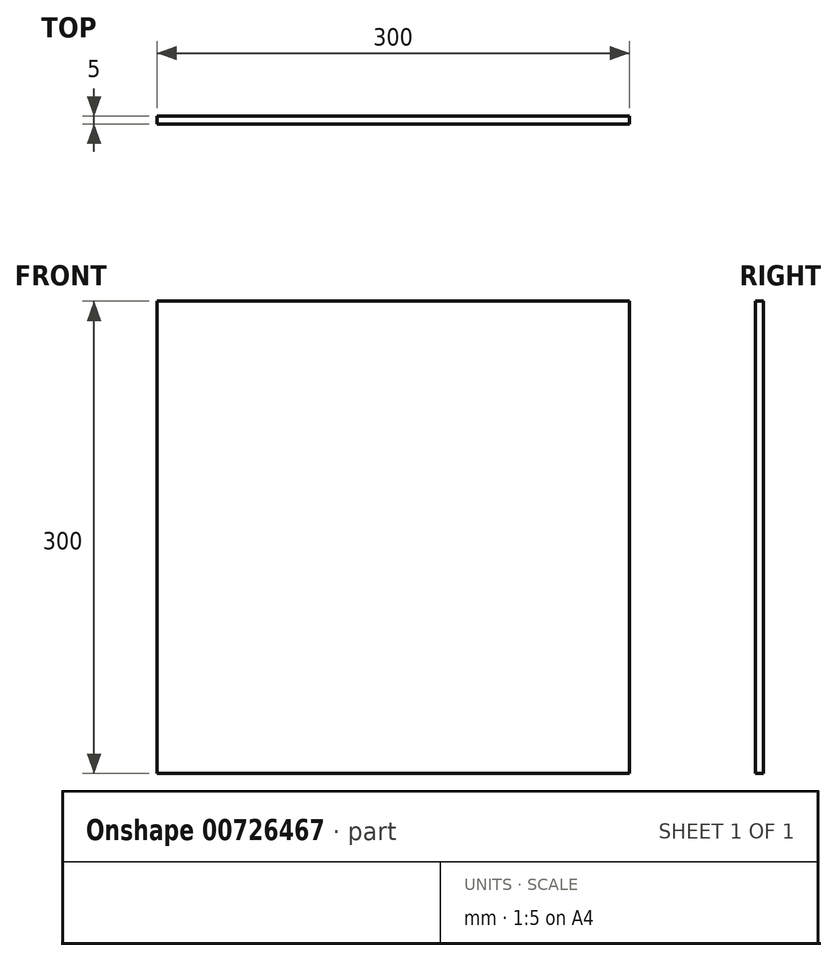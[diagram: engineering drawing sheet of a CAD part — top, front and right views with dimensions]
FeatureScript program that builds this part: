
annotation { "Feature Type Name" : "Feature", "Feature Type Description" : "" }
export const myFeature = defineFeature(function(context is Context, id is Id, definition is map)
    precondition{}
    {
        {
            var Q0;
            Q0=qCreatedBy(makeId("Front.planeOp"),FACE);
            var sketch = newSketch(context, id + "F0", { "sketchPlane" : qUnion([Q0])});
            skLineSegment(sketch, "E0.bottom", {"start": v(0, 0) * mm, "end": v(300, 0) * mm});
            skLineSegment(sketch, "E0.top", {"start": v(0, 300) * mm, "end": v(300, 300) * mm});
            skLineSegment(sketch, "E0.left", {"start": v(0, 0) * mm, "end": v(0, 300) * mm});
            skLineSegment(sketch, "E0.right", {"start": v(300, 0) * mm, "end": v(300, 300) * mm});
            skSolve(sketch);
        }
        {
            var Q0;
            Q0=makeQuery(id+"F0.imprint","IMPRINT",FACE,{"disambiguationData":[TD([[makeQuery(id+"F0.imprint","IMPRINT",EDGE,{"derivedFrom":sQuery(id+"F0.wireOp",EDGE,"E0.bottom")}),1.0]])]});
            extrude(context, id + "F1", {"entities" : qUnion([Q0]), "depth" : 5 * mm, "offsetDistance" : 25 * mm});
        }
    });
